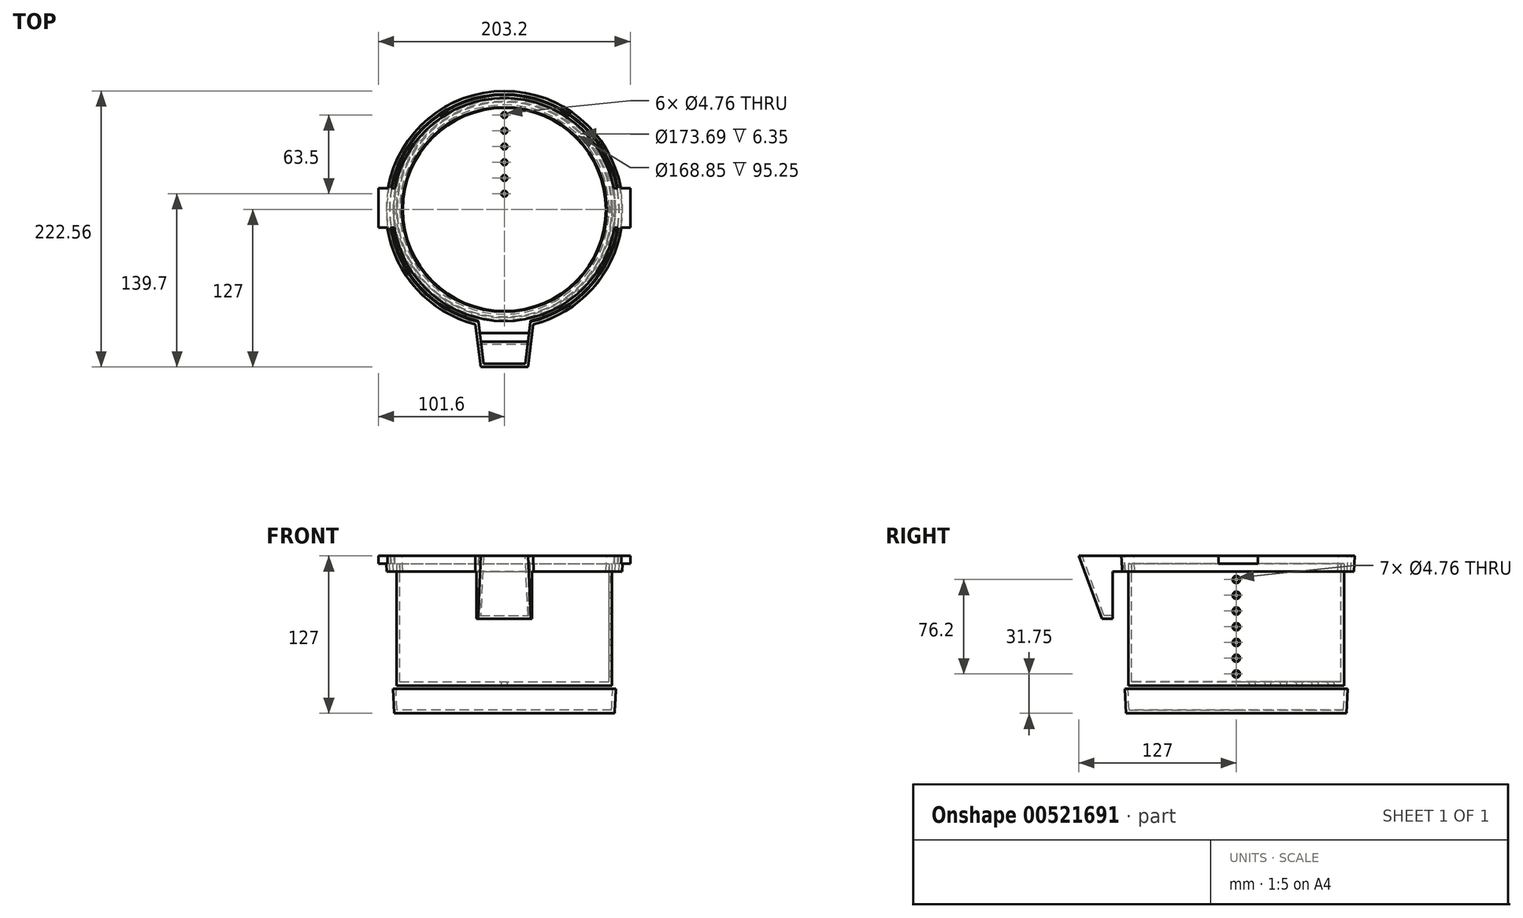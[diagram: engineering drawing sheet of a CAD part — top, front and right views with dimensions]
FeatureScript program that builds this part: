
annotation { "Feature Type Name" : "Feature", "Feature Type Description" : "" }
export const myFeature = defineFeature(function(context is Context, id is Id, definition is map)
    precondition{}
    {
        {
            var Q0;
            Q0=qCreatedBy(makeId("Top.planeOp"),FACE);
            var sketch = newSketch(context, id + "F0", { "sketchPlane" : qUnion([Q0])});
            skCircle(sketch, "E0", {"center": v(0, 0) * mm, "radius": 88.9 * mm});
            skSolve(sketch);
        }
        {
            var Q0;
            Q0 = qSketchRegion(id + "F0", true);
            extrude(context, id + "F1", {"entities" : qUnion([Q0]), "depth" : 127 * mm, "offsetDistance" : 25.4 * mm, "hasDraft" : true, "draftAngle" : 3 * degree});
        }
        {
            var Q0;
            Q0=makeQuery(id+"F1.opExtrude","CAP_FACE",FACE,{"disambiguationData":[OSD([sQuery(id+"F0.wireOp",EDGE,"E0")])],"isStart":false});
            var sketch = newSketch(context, id + "F2", { "sketchPlane" : qUnion([Q0])});
            skLineSegment(sketch, "E1", {"start": v(0, 0) * mm, "end": v(0, -127) * mm, "construction": true});
            skLineSegment(sketch, "E2", {"start": v(-25.4, -76.2) * mm, "end": v(25.4, -76.2) * mm});
            skLineSegment(sketch, "E3", {"start": v(25.4, -76.2) * mm, "end": v(19.05, -127) * mm});
            skLineSegment(sketch, "E4", {"start": v(19.05, -127) * mm, "end": v(-19.05, -127) * mm});
            skLineSegment(sketch, "E5", {"start": v(-19.05, -127) * mm, "end": v(-25.4, -76.2) * mm});
            skSolve(sketch);
        }
        {
            var Q0;
            Q0 = qSketchRegion(id + "F2", true);
            extrude(context, id + "F3", {"entities" : qUnion([Q0]), "operationType" : NewBodyOperationType.ADD, "oppositeDirection" : true, "depth" : 50.8 * mm, "offsetDistance" : 25.4 * mm});
        }
        {
            var Q0;
            Q0=qCreatedBy(makeId("Right.planeOp"),FACE);
            var sketch = newSketch(context, id + "F4", { "sketchPlane" : qUnion([Q0])});
            skLineSegment(sketch, "E6.0", {"start": v(-92.66, 127) * mm, "end": v(-127, 127) * mm, "construction": true});
            skLineSegment(sketch, "E7", {"start": v(-127, 127) * mm, "end": v(-108.4, 76.2) * mm});
            skLineSegment(sketch, "E8.0", {"start": v(-89.82, 76.2) * mm, "end": v(-127, 76.2) * mm, "construction": true});
            skLineSegment(sketch, "E9", {"start": v(-108.4, 76.2) * mm, "end": v(-139.82, 76.2) * mm});
            skLineSegment(sketch, "E10", {"start": v(-139.82, 76.2) * mm, "end": v(-139.82, 127) * mm});
            skLineSegment(sketch, "E11", {"start": v(-139.82, 127) * mm, "end": v(-127, 127) * mm});
            skSolve(sketch);
        }
        {
            var Q0;
            Q0 = qSketchRegion(id + "F4", true);
            extrude(context, id + "F5", {"entities" : qUnion([Q0]), "operationType" : NewBodyOperationType.REMOVE, "endBound" : BoundingType.SYMMETRIC, "oppositeDirection" : true, "depth" : 76.2 * mm, "offsetDistance" : 25.4 * mm});
        }
        {
            var Q0;
            Q0=makeQuery(id+"F3.boolean.opBoolean","MERGE",FACE,{"derivedFrom":[makeQuery(id+"F1.opExtrude","CAP_FACE",FACE,{"disambiguationData":[OSD([sQuery(id+"F0.wireOp",EDGE,"E0")])],"isStart":false}),makeQuery(id+"F3.opExtrude","CAP_FACE",FACE,{"disambiguationData":[OSD([sQuery(id+"F2.wireOp",EDGE,"E2"),sQuery(id+"F2.wireOp",EDGE,"E3"),sQuery(id+"F2.wireOp",EDGE,"E4"),sQuery(id+"F2.wireOp",EDGE,"E5")])],"isStart":true})]});
            shell(context, id + "F6", {"entities" : qUnion([Q0]), "thickness" : 2.54 * mm});
        }
        {
            var Q0;
            Q0=qCreatedBy(makeId("Right.planeOp"),FACE);
            var sketch = newSketch(context, id + "F7", { "sketchPlane" : qUnion([Q0])});
            skLineSegment(sketch, "E12.0", {"start": v(-92.66, 127) * mm, "end": v(95.56, 127) * mm, "construction": true});
            skLineSegment(sketch, "E13.bottom", {"start": v(17.32, 120.65) * mm, "end": v(-14.43, 120.65) * mm});
            skLineSegment(sketch, "E13.top", {"start": v(17.32, 133.35) * mm, "end": v(-14.43, 133.35) * mm});
            skLineSegment(sketch, "E13.left", {"start": v(17.32, 120.65) * mm, "end": v(17.32, 133.35) * mm});
            skLineSegment(sketch, "E13.right", {"start": v(-14.43, 120.65) * mm, "end": v(-14.43, 133.35) * mm});
            skPoint(sketch, "E13.middle", {"position": v(1.45, 127) * mm});
            skSolve(sketch);
        }
        {
            var Q0;
            Q0 = qSketchRegion(id + "F7", true);
            extrude(context, id + "F8", {"entities" : qUnion([Q0]), "operationType" : NewBodyOperationType.REMOVE, "endBound" : BoundingType.SYMMETRIC, "oppositeDirection" : true, "depth" : 304.8 * mm, "offsetDistance" : 25.4 * mm});
        }
        {
            var Q0;
            Q0=qCreatedBy(makeId("Top.planeOp"),FACE);
            cPlane(context, id + "F9", {"entities" : qUnion([Q0]), "cplaneType" : CPlaneType.OFFSET, "offset" : 44.45 * mm, "width" : 152.4 * mm, "height" : 152.4 * mm});
        }
        {
            var Q0;
            Q0=qCreatedBy(id+"F9.planeOp",FACE);
            var sketch = newSketch(context, id + "F10", { "sketchPlane" : qUnion([Q0])});
            skCircle(sketch, "E14", {"center": v(0, 0) * mm, "radius": 85.73 * mm});
            skSolve(sketch);
        }
        {
            var Q0;
            Q0 = qSketchRegion(id + "F10", true);
            extrude(context, id + "F11", {"entities" : qUnion([Q0]), "depth" : 82.55 * mm, "offsetDistance" : 25.4 * mm, "hasDraft" : true, "draftAngle" : 3 * degree});
        }
        {
            var Q0;
            Q0=qCreatedBy(makeId("Right.planeOp"),FACE);
            var sketch = newSketch(context, id + "F12", { "sketchPlane" : qUnion([Q0])});
            skFitSpline(sketch, "E15.0", {"points": [v(17.32, 127) * mm, v(17.32, 124.88) * mm, v(17.32, 122.77) * mm, v(17.32, 120.65) * mm]});
            skLineSegment(sketch, "E15.1", {"start": v(-14.43, 120.65) * mm, "end": v(17.32, 120.65) * mm});
            skLineSegment(sketch, "E16", {"start": v(17.32, 127) * mm, "end": v(-14.43, 127) * mm});
            skLineSegment(sketch, "E17", {"start": v(-14.43, 127) * mm, "end": v(-14.43, 120.65) * mm});
            skSolve(sketch);
        }
        {
            var Q0;
            Q0 = qSketchRegion(id + "F12", true);
            extrude(context, id + "F13", {"entities" : qUnion([Q0]), "operationType" : NewBodyOperationType.ADD, "endBound" : BoundingType.SYMMETRIC, "depth" : 203.2 * mm, "offsetDistance" : 25.4 * mm});
        }
        {
            var Q0;
            Q0=qCreatedBy(makeId("Right.planeOp"),FACE);
            var sketch = newSketch(context, id + "F14", { "sketchPlane" : qUnion([Q0])});
            skLineSegment(sketch, "E18.bottom", {"start": v(-99.83, 114.3) * mm, "end": v(113.17, 114.3) * mm});
            skLineSegment(sketch, "E18.top", {"start": v(-99.83, 19.72) * mm, "end": v(113.17, 19.72) * mm});
            skLineSegment(sketch, "E18.left", {"start": v(-99.83, 114.3) * mm, "end": v(-99.83, 19.72) * mm});
            skLineSegment(sketch, "E18.right", {"start": v(113.17, 114.3) * mm, "end": v(113.17, 19.72) * mm});
            skLineSegment(sketch, "E19.0", {"start": v(17.32, 127) * mm, "end": v(90.05, 127) * mm, "construction": true});
            skSolve(sketch);
        }
        {
            var Q0;
            Q0 = qSketchRegion(id + "F14", true);
            extrude(context, id + "F15", {"entities" : qUnion([Q0]), "operationType" : NewBodyOperationType.REMOVE, "endBound" : BoundingType.SYMMETRIC, "oppositeDirection" : true, "depth" : 3073.4 * mm, "offsetDistance" : 25.4 * mm});
        }
        {
            var Q0;
            Q0=makeQuery(id+"F13.boolean.opBoolean","MERGE",FACE,{"derivedFrom":[makeQuery(id+"F11.opExtrude","CAP_FACE",FACE,{"disambiguationData":[OSD([sQuery(id+"F10.wireOp",EDGE,"E14")])],"isStart":false}),makeQuery(id+"F13.opExtrude","SWEPT_FACE",FACE,{"disambiguationData":[OSD([sQuery(id+"F12.wireOp",EDGE,"E16")])]})]});
            var sketch = newSketch(context, id + "F16", { "sketchPlane" : qUnion([Q0])});
            skCircle(sketch, "E20", {"center": v(0, 0) * mm, "radius": 82.55 * mm});
            skSolve(sketch);
        }
        {
            var Q0;
            Q0 = qSketchRegion(id + "F16", true);
            extrude(context, id + "F17", {"entities" : qUnion([Q0]), "operationType" : NewBodyOperationType.REMOVE, "oppositeDirection" : true, "depth" : 25.4 * mm, "offsetDistance" : 25.4 * mm, "hasDraft" : true, "draftAngle" : 3 * degree, "draftPullDirection" : true});
        }
        {
            var Q0;
            Q0=makeQuery(id+"F15.boolean.opBoolean","COPY",FACE,{"derivedFrom":makeQuery(id+"F15.opExtrude","SWEPT_FACE",FACE,{"disambiguationData":[OSD([sQuery(id+"F14.wireOp",EDGE,"E18.bottom")])]})});
            var sketch = newSketch(context, id + "F18", { "sketchPlane" : qUnion([Q0])});
            skCircle(sketch, "E21.0", {"center": v(0, 0) * mm, "radius": 86.85 * mm});
            skCircle(sketch, "E22.0", {"center": v(0, 0) * mm, "radius": 84.42 * mm});
            skSolve(sketch);
        }
        {
            var Q0;
            Q0 = qSketchRegion(id + "F18", true);
            extrude(context, id + "F19", {"entities" : qUnion([Q0]), "operationType" : NewBodyOperationType.REMOVE, "oppositeDirection" : true, "depth" : 6.35 * mm, "offsetDistance" : 25.4 * mm});
        }
        {
            var Q0;
            Q0=makeQuery(id+"F19.boolean.opBoolean","COPY",FACE,{"derivedFrom":makeQuery(id+"F19.opExtrude","CAP_FACE",FACE,{"disambiguationData":[OSD([sQuery(id+"F18.wireOp",EDGE,"E21.0"),sQuery(id+"F18.wireOp",EDGE,"E22.0")])],"isStart":false})});
            extrude(context, id + "F20", {"entities" : qUnion([Q0]), "depth" : 95.25 * mm, "offsetDistance" : 25.4 * mm});
        }
        {
            var Q0;
            Q0=qCreatedBy(makeId("Right.planeOp"),FACE);
            cPlane(context, id + "F21", {"entities" : qUnion([Q0]), "cplaneType" : CPlaneType.OFFSET, "offset" : 63.5 * mm, "width" : 152.4 * mm, "height" : 152.4 * mm});
        }
        {
            var Q0;
            Q0=qCreatedBy(id+"F21.planeOp",FACE);
            var sketch = newSketch(context, id + "F22", { "sketchPlane" : qUnion([Q0])});
            skCircle(sketch, "E23", {"center": v(0, 107.95) * mm, "radius": 2.38 * mm});
            skCircle(sketch, "E24.0.1.0", {"center": v(0, 95.25) * mm, "radius": 2.38 * mm});
            skCircle(sketch, "E24.0.2.0", {"center": v(0, 82.55) * mm, "radius": 2.38 * mm});
            skCircle(sketch, "E24.0.3.0", {"center": v(0, 69.85) * mm, "radius": 2.38 * mm});
            skCircle(sketch, "E24.0.4.0", {"center": v(0, 57.15) * mm, "radius": 2.38 * mm});
            skCircle(sketch, "E24.0.5.0", {"center": v(0, 44.45) * mm, "radius": 2.38 * mm});
            skCircle(sketch, "E24.0.6.0", {"center": v(0, 31.75) * mm, "radius": 2.38 * mm});
            skCircle(sketch, "E24.1.0.0", {"center": v(114.55, 108.71) * mm, "radius": 2.38 * mm});
            skCircle(sketch, "E24.1.1.0", {"center": v(114.55, 96.01) * mm, "radius": 2.38 * mm});
            skCircle(sketch, "E24.1.2.0", {"center": v(114.55, 83.31) * mm, "radius": 2.38 * mm});
            skCircle(sketch, "E24.1.3.0", {"center": v(114.55, 70.61) * mm, "radius": 2.38 * mm});
            skCircle(sketch, "E24.1.4.0", {"center": v(114.55, 57.91) * mm, "radius": 2.38 * mm});
            skCircle(sketch, "E24.1.5.0", {"center": v(114.55, 45.21) * mm, "radius": 2.38 * mm});
            skCircle(sketch, "E24.1.6.0", {"center": v(114.55, 32.51) * mm, "radius": 2.38 * mm});
            skCircle(sketch, "E24.2.0.0", {"center": v(229.1, 109.47) * mm, "radius": 2.38 * mm});
            skCircle(sketch, "E24.2.1.0", {"center": v(229.1, 96.77) * mm, "radius": 2.38 * mm});
            skCircle(sketch, "E24.2.2.0", {"center": v(229.1, 84.07) * mm, "radius": 2.38 * mm});
            skCircle(sketch, "E24.2.3.0", {"center": v(229.1, 71.37) * mm, "radius": 2.38 * mm});
            skCircle(sketch, "E24.2.4.0", {"center": v(229.1, 58.67) * mm, "radius": 2.38 * mm});
            skCircle(sketch, "E24.2.5.0", {"center": v(229.1, 45.97) * mm, "radius": 2.38 * mm});
            skCircle(sketch, "E24.2.6.0", {"center": v(229.1, 33.27) * mm, "radius": 2.38 * mm});
            skLineSegment(sketch, "E24.direction1", {"start": v(0, 107.95) * mm, "end": v(114.55, 108.71) * mm, "construction": true});
            skLineSegment(sketch, "E24.direction2", {"start": v(0, 107.95) * mm, "end": v(0, 95.25) * mm, "construction": true});
            skSolve(sketch);
        }
        {
            var Q0;
            Q0=makeQuery(id+"F22.imprint","IMPRINT",FACE,{"disambiguationData":[TD([[makeQuery(id+"F22.imprint","IMPRINT",EDGE,{"derivedFrom":sQuery(id+"F22.wireOp",EDGE,"E24.0.1.0")}),1.0]])]});
            var Q1;
            Q1=makeQuery(id+"F22.imprint","IMPRINT",FACE,{"disambiguationData":[TD([[makeQuery(id+"F22.imprint","IMPRINT",EDGE,{"derivedFrom":sQuery(id+"F22.wireOp",EDGE,"E24.0.2.0")}),1.0]])]});
            var Q2;
            Q2=makeQuery(id+"F22.imprint","IMPRINT",FACE,{"disambiguationData":[TD([[makeQuery(id+"F22.imprint","IMPRINT",EDGE,{"derivedFrom":sQuery(id+"F22.wireOp",EDGE,"E23")}),1.0]])]});
            var Q3;
            Q3=makeQuery(id+"F22.imprint","IMPRINT",FACE,{"disambiguationData":[TD([[makeQuery(id+"F22.imprint","IMPRINT",EDGE,{"derivedFrom":sQuery(id+"F22.wireOp",EDGE,"E24.0.3.0")}),1.0]])]});
            var Q4;
            Q4=makeQuery(id+"F22.imprint","IMPRINT",FACE,{"disambiguationData":[TD([[makeQuery(id+"F22.imprint","IMPRINT",EDGE,{"derivedFrom":sQuery(id+"F22.wireOp",EDGE,"E24.0.4.0")}),1.0]])]});
            var Q5;
            Q5=makeQuery(id+"F22.imprint","IMPRINT",FACE,{"disambiguationData":[TD([[makeQuery(id+"F22.imprint","IMPRINT",EDGE,{"derivedFrom":sQuery(id+"F22.wireOp",EDGE,"E24.0.5.0")}),1.0]])]});
            var Q6;
            Q6=makeQuery(id+"F22.imprint","IMPRINT",FACE,{"disambiguationData":[TD([[makeQuery(id+"F22.imprint","IMPRINT",EDGE,{"derivedFrom":sQuery(id+"F22.wireOp",EDGE,"E24.0.6.0")}),1.0]])]});
            extrude(context, id + "F23", {"entities" : qUnion([Q0, Q1, Q2, Q3, Q4, Q5, Q6]), "operationType" : NewBodyOperationType.REMOVE, "depth" : 25.4 * mm, "offsetDistance" : 25.4 * mm});
        }
        {
            var Q0;
            Q0=makeQuery(id+"F23.boolean.opBoolean","COPY",FACE,{"derivedFrom":makeQuery(id+"F23.opExtrude","SWEPT_FACE",FACE,{"disambiguationData":[OSD([sQuery(id+"F22.wireOp",EDGE,"E23")])]})});
            var Q1;
            Q1=makeQuery(id+"F23.boolean.opBoolean","COPY",FACE,{"derivedFrom":makeQuery(id+"F23.opExtrude","SWEPT_FACE",FACE,{"disambiguationData":[OSD([sQuery(id+"F22.wireOp",EDGE,"E24.0.1.0")])]})});
            var Q2;
            Q2=makeQuery(id+"F23.boolean.opBoolean","COPY",FACE,{"derivedFrom":makeQuery(id+"F23.opExtrude","SWEPT_FACE",FACE,{"disambiguationData":[OSD([sQuery(id+"F22.wireOp",EDGE,"E24.0.2.0")])]})});
            var Q3;
            Q3=makeQuery(id+"F23.boolean.opBoolean","COPY",FACE,{"derivedFrom":makeQuery(id+"F23.opExtrude","SWEPT_FACE",FACE,{"disambiguationData":[OSD([sQuery(id+"F22.wireOp",EDGE,"E24.0.3.0")])]})});
            var Q4;
            Q4=makeQuery(id+"F23.boolean.opBoolean","COPY",FACE,{"derivedFrom":makeQuery(id+"F23.opExtrude","SWEPT_FACE",FACE,{"disambiguationData":[OSD([sQuery(id+"F22.wireOp",EDGE,"E24.0.4.0")])]})});
            var Q5;
            Q5=makeQuery(id+"F23.boolean.opBoolean","COPY",FACE,{"derivedFrom":makeQuery(id+"F23.opExtrude","SWEPT_FACE",FACE,{"disambiguationData":[OSD([sQuery(id+"F22.wireOp",EDGE,"E24.0.5.0")])]})});
            var Q6;
            Q6=makeQuery(id+"F23.boolean.opBoolean","COPY",FACE,{"derivedFrom":makeQuery(id+"F23.opExtrude","SWEPT_FACE",FACE,{"disambiguationData":[OSD([sQuery(id+"F22.wireOp",EDGE,"E24.0.6.0")])]})});
            var Q7;
            Q7=makeQuery(id+"F23.boolean.opBoolean","INTERSECT",EDGE,{"derivedFrom":[makeQuery(id+"F20.opExtrude","SWEPT_FACE",FACE,{"disambiguationData":[OSD([sQuery(id+"F18.wireOp",EDGE,"E21.0")])]}),makeQuery(id+"F23.opExtrude","SWEPT_FACE",FACE,{"disambiguationData":[OSD([sQuery(id+"F22.wireOp",EDGE,"E23")])]})]});
            var Q8;
            Q8=makeQuery(id+"F23.boolean.opBoolean","INTERSECT",EDGE,{"derivedFrom":[makeQuery(id+"F20.opExtrude","SWEPT_FACE",FACE,{"disambiguationData":[OSD([sQuery(id+"F18.wireOp",EDGE,"E21.0")])]}),makeQuery(id+"F23.opExtrude","SWEPT_FACE",FACE,{"disambiguationData":[OSD([sQuery(id+"F22.wireOp",EDGE,"E24.0.1.0")])]})]});
            var Q9;
            Q9=makeQuery(id+"F23.boolean.opBoolean","INTERSECT",EDGE,{"derivedFrom":[makeQuery(id+"F20.opExtrude","SWEPT_FACE",FACE,{"disambiguationData":[OSD([sQuery(id+"F18.wireOp",EDGE,"E21.0")])]}),makeQuery(id+"F23.opExtrude","SWEPT_FACE",FACE,{"disambiguationData":[OSD([sQuery(id+"F22.wireOp",EDGE,"E24.0.2.0")])]})]});
            var Q10;
            Q10=makeQuery(id+"F23.boolean.opBoolean","INTERSECT",EDGE,{"derivedFrom":[makeQuery(id+"F20.opExtrude","SWEPT_FACE",FACE,{"disambiguationData":[OSD([sQuery(id+"F18.wireOp",EDGE,"E21.0")])]}),makeQuery(id+"F23.opExtrude","SWEPT_FACE",FACE,{"disambiguationData":[OSD([sQuery(id+"F22.wireOp",EDGE,"E24.0.3.0")])]})]});
            var Q11;
            Q11=makeQuery(id+"F23.boolean.opBoolean","INTERSECT",EDGE,{"derivedFrom":[makeQuery(id+"F20.opExtrude","SWEPT_FACE",FACE,{"disambiguationData":[OSD([sQuery(id+"F18.wireOp",EDGE,"E21.0")])]}),makeQuery(id+"F23.opExtrude","SWEPT_FACE",FACE,{"disambiguationData":[OSD([sQuery(id+"F22.wireOp",EDGE,"E24.0.4.0")])]})]});
            var Q12;
            Q12=makeQuery(id+"F23.boolean.opBoolean","INTERSECT",EDGE,{"derivedFrom":[makeQuery(id+"F20.opExtrude","SWEPT_FACE",FACE,{"disambiguationData":[OSD([sQuery(id+"F18.wireOp",EDGE,"E21.0")])]}),makeQuery(id+"F23.opExtrude","SWEPT_FACE",FACE,{"disambiguationData":[OSD([sQuery(id+"F22.wireOp",EDGE,"E24.0.5.0")])]})]});
            var Q13;
            Q13=makeQuery(id+"F23.boolean.opBoolean","INTERSECT",EDGE,{"derivedFrom":[makeQuery(id+"F20.opExtrude","SWEPT_FACE",FACE,{"disambiguationData":[OSD([sQuery(id+"F18.wireOp",EDGE,"E21.0")])]}),makeQuery(id+"F23.opExtrude","SWEPT_FACE",FACE,{"disambiguationData":[OSD([sQuery(id+"F22.wireOp",EDGE,"E24.0.6.0")])]})]});
            var Q14;
            Q14=makeQuery(id+"F23.boolean.opBoolean","INTERSECT",EDGE,{"derivedFrom":[makeQuery(id+"F20.opExtrude","SWEPT_FACE",FACE,{"disambiguationData":[OSD([sQuery(id+"F18.wireOp",EDGE,"E22.0")])]}),makeQuery(id+"F23.opExtrude","SWEPT_FACE",FACE,{"disambiguationData":[OSD([sQuery(id+"F22.wireOp",EDGE,"E23")])]})]});
            var Q15;
            Q15=makeQuery(id+"F23.boolean.opBoolean","INTERSECT",EDGE,{"derivedFrom":[makeQuery(id+"F20.opExtrude","SWEPT_FACE",FACE,{"disambiguationData":[OSD([sQuery(id+"F18.wireOp",EDGE,"E22.0")])]}),makeQuery(id+"F23.opExtrude","SWEPT_FACE",FACE,{"disambiguationData":[OSD([sQuery(id+"F22.wireOp",EDGE,"E24.0.1.0")])]})]});
            var Q16;
            Q16=makeQuery(id+"F23.boolean.opBoolean","INTERSECT",EDGE,{"derivedFrom":[makeQuery(id+"F20.opExtrude","SWEPT_FACE",FACE,{"disambiguationData":[OSD([sQuery(id+"F18.wireOp",EDGE,"E22.0")])]}),makeQuery(id+"F23.opExtrude","SWEPT_FACE",FACE,{"disambiguationData":[OSD([sQuery(id+"F22.wireOp",EDGE,"E24.0.2.0")])]})]});
            var Q17;
            Q17=makeQuery(id+"F23.boolean.opBoolean","INTERSECT",EDGE,{"derivedFrom":[makeQuery(id+"F20.opExtrude","SWEPT_FACE",FACE,{"disambiguationData":[OSD([sQuery(id+"F18.wireOp",EDGE,"E22.0")])]}),makeQuery(id+"F23.opExtrude","SWEPT_FACE",FACE,{"disambiguationData":[OSD([sQuery(id+"F22.wireOp",EDGE,"E24.0.3.0")])]})]});
            var Q18;
            Q18=makeQuery(id+"F23.boolean.opBoolean","INTERSECT",EDGE,{"derivedFrom":[makeQuery(id+"F20.opExtrude","SWEPT_FACE",FACE,{"disambiguationData":[OSD([sQuery(id+"F18.wireOp",EDGE,"E22.0")])]}),makeQuery(id+"F23.opExtrude","SWEPT_FACE",FACE,{"disambiguationData":[OSD([sQuery(id+"F22.wireOp",EDGE,"E24.0.4.0")])]})]});
            var Q19;
            Q19=makeQuery(id+"F23.boolean.opBoolean","INTERSECT",EDGE,{"derivedFrom":[makeQuery(id+"F20.opExtrude","SWEPT_FACE",FACE,{"disambiguationData":[OSD([sQuery(id+"F18.wireOp",EDGE,"E22.0")])]}),makeQuery(id+"F23.opExtrude","SWEPT_FACE",FACE,{"disambiguationData":[OSD([sQuery(id+"F22.wireOp",EDGE,"E24.0.5.0")])]})]});
            fillet(context, id + "F24", {"entities" : qUnion([Q0, Q1, Q2, Q3, Q4, Q5, Q6, Q7, Q8, Q9, Q10, Q11, Q12, Q13, Q14, Q15, Q16, Q17, Q18, Q19]), "radius" : 0.5 * mm, "tangentPropagation" : true, "allowEdgeOverflow" : false});
        }
        {
            var Q0;
            Q0=makeQuery(id+"F20.opExtrude","CAP_FACE",FACE,{"disambiguationData":[OSD([sQuery(id+"F18.wireOp",EDGE,"E21.0"),sQuery(id+"F18.wireOp",EDGE,"E22.0")])],"isStart":false});
            var sketch = newSketch(context, id + "F25", { "sketchPlane" : qUnion([Q0])});
            skSolve(sketch);
        }
        {
            var Q0;
            Q0=makeQuery(id+"F25.imprint","IMPRINT",FACE,{"disambiguationData":[TD([[makeQuery(id+"F25.imprint","IMPRINT",EDGE,{"derivedFrom":makeQuery(id+"F20.opExtrude","CAP_EDGE",EDGE,{"disambiguationData":[OSD([sQuery(id+"F18.wireOp",EDGE,"E21.0")])],"isStart":false})}),1.0]])]});
            var sketch = newSketch(context, id + "F26", { "sketchPlane" : qUnion([Q0])});
            skCircle(sketch, "E25.0", {"center": v(0, 0) * mm, "radius": 86.85 * mm});
            skSolve(sketch);
        }
        {
            var Q0;
            Q0 = qSketchRegion(id + "F26", true);
            extrude(context, id + "F27", {"entities" : qUnion([Q0]), "operationType" : NewBodyOperationType.ADD, "depth" : 3.17 * mm, "offsetDistance" : 25.4 * mm});
        }
        {
            var Q0;
            Q0=makeQuery(id+"F27.opExtrude","CAP_FACE",FACE,{"disambiguationData":[OSD([sQuery(id+"F26.wireOp",EDGE,"E25.0")])],"isStart":false});
            var sketch = newSketch(context, id + "F28", { "sketchPlane" : qUnion([Q0])});
            skCircle(sketch, "E26", {"center": v(0, -12.7) * mm, "radius": 2.38 * mm});
            skCircle(sketch, "E27.0.1.0", {"center": v(0, -25.4) * mm, "radius": 2.38 * mm});
            skCircle(sketch, "E27.0.2.0", {"center": v(0, -38.1) * mm, "radius": 2.38 * mm});
            skCircle(sketch, "E27.0.3.0", {"center": v(0, -50.8) * mm, "radius": 2.38 * mm});
            skCircle(sketch, "E27.0.4.0", {"center": v(0, -63.5) * mm, "radius": 2.38 * mm});
            skCircle(sketch, "E27.0.5.0", {"center": v(0, -76.2) * mm, "radius": 2.38 * mm});
            skCircle(sketch, "E27.1.0.0", {"center": v(287.02, -32.26) * mm, "radius": 2.38 * mm});
            skCircle(sketch, "E27.1.1.0", {"center": v(287.02, -44.96) * mm, "radius": 2.38 * mm});
            skCircle(sketch, "E27.1.2.0", {"center": v(287.02, -57.66) * mm, "radius": 2.38 * mm});
            skCircle(sketch, "E27.1.3.0", {"center": v(287.02, -70.36) * mm, "radius": 2.38 * mm});
            skCircle(sketch, "E27.1.4.0", {"center": v(287.02, -83.06) * mm, "radius": 2.38 * mm});
            skCircle(sketch, "E27.1.5.0", {"center": v(287.02, -95.76) * mm, "radius": 2.38 * mm});
            skCircle(sketch, "E27.2.0.0", {"center": v(574.04, -51.82) * mm, "radius": 2.38 * mm});
            skCircle(sketch, "E27.2.1.0", {"center": v(574.04, -64.52) * mm, "radius": 2.38 * mm});
            skCircle(sketch, "E27.2.2.0", {"center": v(574.04, -77.22) * mm, "radius": 2.38 * mm});
            skCircle(sketch, "E27.2.3.0", {"center": v(574.04, -89.92) * mm, "radius": 2.38 * mm});
            skCircle(sketch, "E27.2.4.0", {"center": v(574.04, -102.62) * mm, "radius": 2.38 * mm});
            skCircle(sketch, "E27.2.5.0", {"center": v(574.04, -115.32) * mm, "radius": 2.38 * mm});
            skLineSegment(sketch, "E27.direction1", {"start": v(0, -12.7) * mm, "end": v(287.02, -32.26) * mm, "construction": true});
            skLineSegment(sketch, "E27.direction2", {"start": v(0, -12.7) * mm, "end": v(0, -25.4) * mm, "construction": true});
            skSolve(sketch);
        }
        {
            var Q0;
            Q0 = qSketchRegion(id + "F28", true);
            extrude(context, id + "F29", {"entities" : qUnion([Q0]), "operationType" : NewBodyOperationType.REMOVE, "oppositeDirection" : true, "depth" : 25.4 * mm, "offsetDistance" : 25.4 * mm});
        }
        {
            var Q0;
            Q0=makeQuery(id+"F29.boolean.opBoolean","INTERSECT",EDGE,{"derivedFrom":[makeQuery(id+"F27.opExtrude","CAP_FACE",FACE,{"disambiguationData":[OSD([sQuery(id+"F26.wireOp",EDGE,"E25.0")])],"isStart":true}),makeQuery(id+"F29.opExtrude","SWEPT_FACE",FACE,{"disambiguationData":[OSD([sQuery(id+"F28.wireOp",EDGE,"E27.0.1.0")])]})]});
            var Q1;
            Q1=makeQuery(id+"F29.boolean.opBoolean","COPY",EDGE,{"derivedFrom":makeQuery(id+"F29.opExtrude","CAP_EDGE",EDGE,{"disambiguationData":[OSD([sQuery(id+"F28.wireOp",EDGE,"E27.0.1.0")])],"isStart":true})});
            var Q2;
            Q2=makeQuery(id+"F29.boolean.opBoolean","INTERSECT",EDGE,{"derivedFrom":[makeQuery(id+"F27.opExtrude","CAP_FACE",FACE,{"disambiguationData":[OSD([sQuery(id+"F26.wireOp",EDGE,"E25.0")])],"isStart":true}),makeQuery(id+"F29.opExtrude","SWEPT_FACE",FACE,{"disambiguationData":[OSD([sQuery(id+"F28.wireOp",EDGE,"E26")])]})]});
            var Q3;
            Q3=makeQuery(id+"F29.boolean.opBoolean","COPY",EDGE,{"derivedFrom":makeQuery(id+"F29.opExtrude","CAP_EDGE",EDGE,{"disambiguationData":[OSD([sQuery(id+"F28.wireOp",EDGE,"E26")])],"isStart":true})});
            var Q4;
            Q4=makeQuery(id+"F29.boolean.opBoolean","COPY",EDGE,{"derivedFrom":makeQuery(id+"F29.opExtrude","CAP_EDGE",EDGE,{"disambiguationData":[OSD([sQuery(id+"F28.wireOp",EDGE,"E27.0.2.0")])],"isStart":true})});
            var Q5;
            Q5=makeQuery(id+"F29.boolean.opBoolean","INTERSECT",EDGE,{"derivedFrom":[makeQuery(id+"F27.opExtrude","CAP_FACE",FACE,{"disambiguationData":[OSD([sQuery(id+"F26.wireOp",EDGE,"E25.0")])],"isStart":true}),makeQuery(id+"F29.opExtrude","SWEPT_FACE",FACE,{"disambiguationData":[OSD([sQuery(id+"F28.wireOp",EDGE,"E27.0.2.0")])]})]});
            var Q6;
            Q6=makeQuery(id+"F29.boolean.opBoolean","COPY",EDGE,{"derivedFrom":makeQuery(id+"F29.opExtrude","CAP_EDGE",EDGE,{"disambiguationData":[OSD([sQuery(id+"F28.wireOp",EDGE,"E27.0.3.0")])],"isStart":true})});
            var Q7;
            Q7=makeQuery(id+"F29.boolean.opBoolean","INTERSECT",EDGE,{"derivedFrom":[makeQuery(id+"F27.opExtrude","CAP_FACE",FACE,{"disambiguationData":[OSD([sQuery(id+"F26.wireOp",EDGE,"E25.0")])],"isStart":true}),makeQuery(id+"F29.opExtrude","SWEPT_FACE",FACE,{"disambiguationData":[OSD([sQuery(id+"F28.wireOp",EDGE,"E27.0.3.0")])]})]});
            var Q8;
            Q8=makeQuery(id+"F29.boolean.opBoolean","COPY",EDGE,{"derivedFrom":makeQuery(id+"F29.opExtrude","CAP_EDGE",EDGE,{"disambiguationData":[OSD([sQuery(id+"F28.wireOp",EDGE,"E27.0.4.0")])],"isStart":true})});
            var Q9;
            Q9=makeQuery(id+"F29.boolean.opBoolean","INTERSECT",EDGE,{"derivedFrom":[makeQuery(id+"F27.opExtrude","CAP_FACE",FACE,{"disambiguationData":[OSD([sQuery(id+"F26.wireOp",EDGE,"E25.0")])],"isStart":true}),makeQuery(id+"F29.opExtrude","SWEPT_FACE",FACE,{"disambiguationData":[OSD([sQuery(id+"F28.wireOp",EDGE,"E27.0.4.0")])]})]});
            var Q10;
            Q10=makeQuery(id+"F29.boolean.opBoolean","COPY",EDGE,{"derivedFrom":makeQuery(id+"F29.opExtrude","CAP_EDGE",EDGE,{"disambiguationData":[OSD([sQuery(id+"F28.wireOp",EDGE,"E27.0.5.0")])],"isStart":true})});
            var Q11;
            Q11=makeQuery(id+"F29.boolean.opBoolean","INTERSECT",EDGE,{"derivedFrom":[makeQuery(id+"F27.opExtrude","CAP_FACE",FACE,{"disambiguationData":[OSD([sQuery(id+"F26.wireOp",EDGE,"E25.0")])],"isStart":true}),makeQuery(id+"F29.opExtrude","SWEPT_FACE",FACE,{"disambiguationData":[OSD([sQuery(id+"F28.wireOp",EDGE,"E27.0.5.0")])]})]});
            fillet(context, id + "F30", {"entities" : qUnion([Q0, Q1, Q2, Q3, Q4, Q5, Q6, Q7, Q8, Q9, Q10, Q11]), "radius" : 1.27 * mm, "tangentPropagation" : true, "allowEdgeOverflow" : false});
        }
    });
